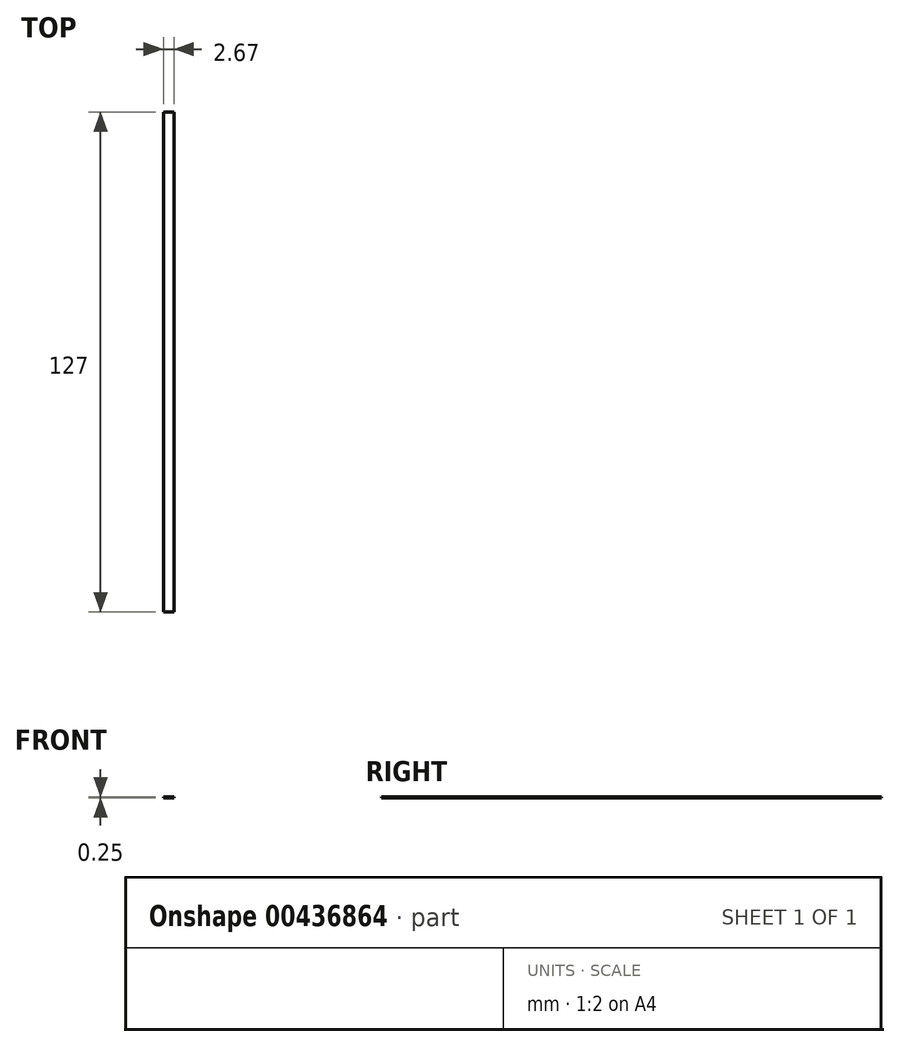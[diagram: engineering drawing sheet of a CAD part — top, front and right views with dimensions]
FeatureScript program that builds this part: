
annotation { "Feature Type Name" : "Feature", "Feature Type Description" : "" }
export const myFeature = defineFeature(function(context is Context, id is Id, definition is map)
    precondition{}
    {
        {
            var Q0;
            Q0=qCreatedBy(makeId("Top.planeOp"),FACE);
            var sketch = newSketch(context, id + "F0", { "sketchPlane" : qUnion([Q0])});
            skLineSegment(sketch, "E0.bottom", {"start": v(0, 0) * mm, "end": v(2.67, 0) * mm});
            skLineSegment(sketch, "E0.top", {"start": v(0, 127) * mm, "end": v(2.67, 127) * mm});
            skLineSegment(sketch, "E0.left", {"start": v(0, 0) * mm, "end": v(0, 127) * mm});
            skLineSegment(sketch, "E0.right", {"start": v(2.67, 0) * mm, "end": v(2.67, 127) * mm});
            skSolve(sketch);
        }
        {
            var Q0;
            Q0 = qSketchRegion(id + "F0", true);
            extrude(context, id + "F1", {"entities" : qUnion([Q0]), "depth" : 0.25 * mm});
        }
    });
